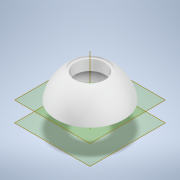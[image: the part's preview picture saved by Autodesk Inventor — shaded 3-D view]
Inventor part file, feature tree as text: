
AUTODESK INVENTOR PART (.ipt)
format: ipt  version: 2021 (Build 250183000, 183)  size: 457,216 bytes
history: native  units: in
note: dims shown in document units (in); Inventor stores cm internally (conversion verified against a paired STEP export)
features: sketch x8, extrude x7, fillet x2, plane x2, other x1, revolve x1, pattern_circular x1, mirror x1, chamfer x1
ambient origin geometry x8: Origin, YZ Plane, XZ Plane, XY Plane, X Axis, Y Axis, Z Axis, Center Point
bodies: Solid1 (feature_tree)
feature tree (24):
  extrude  "Extrusion1"  Depth=1.0236in
  other  "Work Axis1"
  revolve  "Revolution1"  [1 undecoded]
  extrude  "Extrusion2"  Depth=1.0079in
  extrude  "Extrusion3"  TaperAngle=90.0deg  [1 undecoded]
  extrude  "Extrusion4"  Depth=0.8976in
  extrude  "Extrusion5"  Depth=1.0236in TaperAngle=0.0deg
  pattern_circular  "Circular Pattern1"  [2 undecoded]
  mirror  "Mirror1"
  fillet  "Fillet2"  Radius=0.1969in
  extrude  "Extrusion7"  Depth=0.3937in TaperAngle=240.0deg
  chamfer  "Chamfer2"  Distance=0.5039in
  fillet  "Fillet3"  Radius=0.0394in
  plane  "Work Plane4"
  extrude  "Extrusion12"  Depth=0.3937in
  sketch  "Sketch1"  dims[d0=2.0472in d1=1.0236in]
  sketch  "Sketch2"  dims[d2=1.0236in d3=1.0236in]
  sketch  "Sketch3"  dims[d4=1.378in d5=0.0in d6=1.0079in]
  sketch  "Sketch4"  dims[d7=90.0deg d8=90.0deg]
  sketch  "Sketch5"  dims[d9=0.0394in d10=0.0in d11=0.8976in]
  sketch  "Sketch8"  dims[d12=0.0in d13=0.0in d14=1.0236in d15=0.0in]
  sketch  "Sketch10"  dims[d16=1.2913in]
  plane  "Work Plane2"
  sketch  "Sketch15"  dims[d21=0.2126in d22=0.8268in d23=0.1969in d24=0.0in d25=1.9685in d26=240.0deg d33=0.5039in d34=0.0394in d35=0.7079in d36=0.3937in d37=0.3539in d38=0.2362in d39=0.3937in d40=0.0in d41=0.3937in d42=0.2283in d43=45.0deg d44=0.1969in d48=0.0in d56=-0.5906in d57=0.0in d58=0.0in d45=0.0197in d46=0.0344in d47=0.0197in]
note: 4 required parameter values undecoded (feature->parameter linkage not recoverable at this tier; creation-order binding heuristic only, values carry confidence <= 0.55)